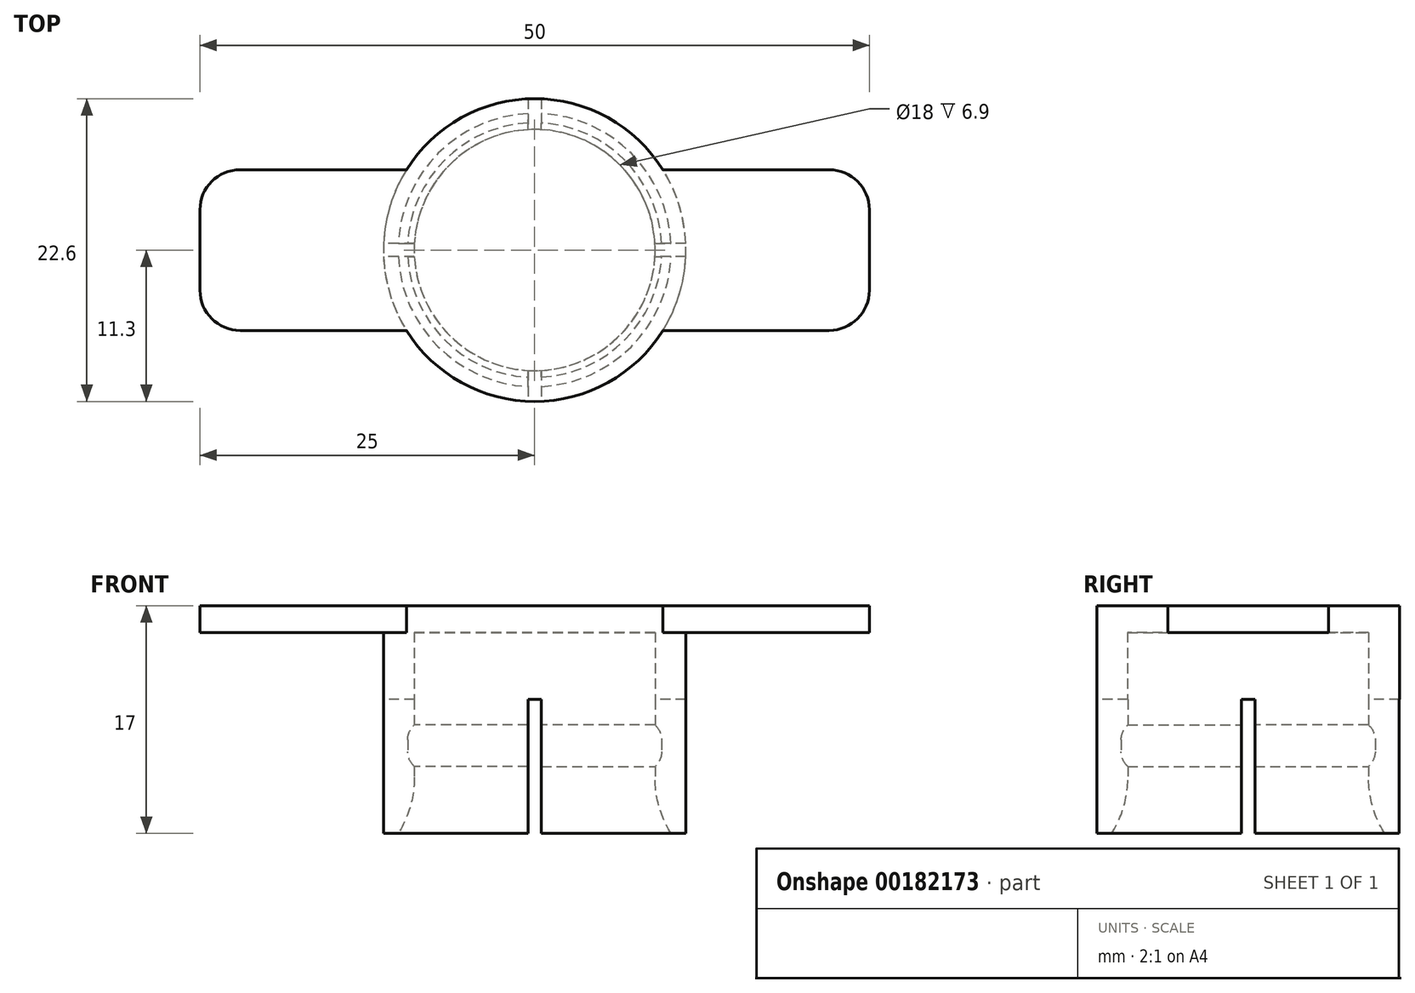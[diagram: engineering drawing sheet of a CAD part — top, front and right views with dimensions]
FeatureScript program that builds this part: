
annotation { "Feature Type Name" : "Feature", "Feature Type Description" : "" }
export const myFeature = defineFeature(function(context is Context, id is Id, definition is map)
    precondition{}
    {
        {
            var Q0;
            Q0=qCreatedBy(makeId("Top.planeOp"),FACE);
            var sketch = newSketch(context, id + "F0", { "sketchPlane" : qUnion([Q0])});
            skCircle(sketch, "E0", {"center": v(0, 0) * mm, "radius": 11.3 * mm});
            skCircle(sketch, "E1", {"center": v(0, 0) * mm, "radius": 9 * mm});
            skSolve(sketch);
        }
        {
            var Q0;
            Q0 = qSketchRegion(id + "F0", true);
            extrude(context, id + "F1", {"entities" : qUnion([Q0]), "depth" : 15 * mm});
        }
        {
            var Q0;
            Q0=makeQuery(id+"F1.opExtrude","CAP_FACE",FACE,{"disambiguationData":[OSD([sQuery(id+"F0.wireOp",EDGE,"E0"),sQuery(id+"F0.wireOp",EDGE,"E1")])],"isStart":false});
            var sketch = newSketch(context, id + "F2", { "sketchPlane" : qUnion([Q0])});
            skCircle(sketch, "E2.0", {"center": v(0, 0) * mm, "radius": 11.3 * mm});
            skSolve(sketch);
        }
        {
            var Q0;
            Q0 = qSketchRegion(id + "F2", true);
            extrude(context, id + "F3", {"entities" : qUnion([Q0]), "operationType" : NewBodyOperationType.ADD, "depth" : 2 * mm});
        }
        {
            var Q0;
            Q0=makeQuery(id+"F1.opExtrude","CAP_FACE",FACE,{"disambiguationData":[OSD([sQuery(id+"F0.wireOp",EDGE,"E0"),sQuery(id+"F0.wireOp",EDGE,"E1")])],"isStart":true});
            var sketch = newSketch(context, id + "F4", { "sketchPlane" : qUnion([Q0])});
            skCircle(sketch, "E3", {"center": v(0, 0) * mm, "radius": 9.5 * mm});
            skCircle(sketch, "E4", {"center": v(0, 0) * mm, "radius": 7.14 * mm});
            skSolve(sketch);
        }
        {
            var Q0;
            Q0 = qSketchRegion(id + "F4", true);
            extrude(context, id + "F5", {"entities" : qUnion([Q0]), "operationType" : NewBodyOperationType.REMOVE, "oppositeDirection" : true, "depth" : 8.1 * mm, "hasSecondDirection" : true, "secondDirectionOppositeDirection" : true, "secondDirectionDepth" : 5 * mm});
        }
        {
            var Q0;
            Q0=makeQuery(id+"F5.boolean.opBoolean","COPY",FACE,{"derivedFrom":makeQuery(id+"F5.opExtrude","SWEPT_FACE",FACE,{"disambiguationData":[OSD([sQuery(id+"F4.wireOp",EDGE,"E3")])]})});
            fillet(context, id + "F6", {"entities" : qUnion([Q0]), "radius" : 1.5 * mm, "tangentPropagation" : true, "allowEdgeOverflow" : false});
        }
        {
            var Q0;
            Q0=makeQuery(id+"F3.opExtrude","CAP_FACE",FACE,{"disambiguationData":[OSD([sQuery(id+"F2.wireOp",EDGE,"E2.0")])],"isStart":false});
            var sketch = newSketch(context, id + "F7", { "sketchPlane" : qUnion([Q0])});
            skLineSegment(sketch, "E5.bottom", {"start": v(25, -6) * mm, "end": v(-25, -6) * mm});
            skLineSegment(sketch, "E5.top", {"start": v(25, 6) * mm, "end": v(-25, 6) * mm});
            skLineSegment(sketch, "E5.left", {"start": v(25, -6) * mm, "end": v(25, 6) * mm});
            skLineSegment(sketch, "E5.right", {"start": v(-25, -6) * mm, "end": v(-25, 6) * mm});
            skPoint(sketch, "E5.middle", {"position": v(0, 0) * mm});
            skSolve(sketch);
        }
        {
            var Q0;
            Q0 = qSketchRegion(id + "F7", true);
            extrude(context, id + "F8", {"entities" : qUnion([Q0]), "operationType" : NewBodyOperationType.ADD, "oppositeDirection" : true, "depth" : 2 * mm});
        }
        {
            var Q0;
            Q0=makeQuery(id+"F8.opExtrude","SWEPT_EDGE",EDGE,{"disambiguationData":[OSD([sQuery(id+"F7.wireOp",EDGE,"E5.top"),sQuery(id+"F7.wireOp",EDGE,"E5.right")])]});
            var Q1;
            Q1=makeQuery(id+"F8.opExtrude","SWEPT_EDGE",EDGE,{"disambiguationData":[OSD([sQuery(id+"F7.wireOp",EDGE,"E5.bottom"),sQuery(id+"F7.wireOp",EDGE,"E5.right")])]});
            var Q2;
            Q2=makeQuery(id+"F8.opExtrude","SWEPT_EDGE",EDGE,{"disambiguationData":[OSD([sQuery(id+"F7.wireOp",EDGE,"E5.top"),sQuery(id+"F7.wireOp",EDGE,"E5.left")])]});
            var Q3;
            Q3=makeQuery(id+"F8.opExtrude","SWEPT_EDGE",EDGE,{"disambiguationData":[OSD([sQuery(id+"F7.wireOp",EDGE,"E5.bottom"),sQuery(id+"F7.wireOp",EDGE,"E5.left")])]});
            fillet(context, id + "F9", {"entities" : qUnion([Q0, Q1, Q2, Q3]), "radius" : 3 * mm, "tangentPropagation" : true, "allowEdgeOverflow" : false});
        }
        {
            var Q0;
            Q0=makeQuery(id+"F1.opExtrude","CAP_FACE",FACE,{"disambiguationData":[OSD([sQuery(id+"F0.wireOp",EDGE,"E0"),sQuery(id+"F0.wireOp",EDGE,"E1")])],"isStart":true});
            var sketch = newSketch(context, id + "F10", { "sketchPlane" : qUnion([Q0])});
            skLineSegment(sketch, "E6.bottom", {"start": v(-0.5, -12.5) * mm, "end": v(0.5, -12.5) * mm});
            skLineSegment(sketch, "E6.top", {"start": v(-0.5, 12.5) * mm, "end": v(0.5, 12.5) * mm});
            skLineSegment(sketch, "E6.left", {"start": v(-0.5, -12.5) * mm, "end": v(-0.5, 12.5) * mm});
            skLineSegment(sketch, "E6.right", {"start": v(0.5, -12.5) * mm, "end": v(0.5, 12.5) * mm});
            skPoint(sketch, "E6.middle", {"position": v(0, 0) * mm});
            skLineSegment(sketch, "E7.bottom", {"start": v(12.5, 0.5) * mm, "end": v(-12.5, 0.5) * mm});
            skLineSegment(sketch, "E7.top", {"start": v(12.5, -0.5) * mm, "end": v(-12.5, -0.5) * mm});
            skLineSegment(sketch, "E7.left", {"start": v(12.5, 0.5) * mm, "end": v(12.5, -0.5) * mm});
            skLineSegment(sketch, "E7.right", {"start": v(-12.5, 0.5) * mm, "end": v(-12.5, -0.5) * mm});
            skSolve(sketch);
        }
        {
            var Q0;
            Q0 = qSketchRegion(id + "F10", true);
            extrude(context, id + "F11", {"entities" : qUnion([Q0]), "operationType" : NewBodyOperationType.REMOVE, "oppositeDirection" : true, "depth" : 10 * mm});
        }
        {
            var Q0;
            {var subQ0=sQuery(id+"F0.wireOp",EDGE,"E1");var subQ1=sQuery(id+"F0.wireOp",EDGE,"E0");var subQ2=sQuery(id+"F10.wireOp",EDGE,"E7.bottom");var subQ3=sQuery(id+"F10.wireOp",EDGE,"E6.right");var subQ4=makeQuery(id+"F10.imprint","INTERSECT",VERTEX,{"derivedFrom":[subQ3,subQ2]});var subQ5=makeQuery(id+"F1.opExtrude","CAP_EDGE",EDGE,{"disambiguationData":[OSD([subQ0])],"isStart":true});var subQ7=makeQuery(id+"F1.opExtrude","CAP_EDGE",EDGE,{"disambiguationData":[OSD([subQ1])],"isStart":true});var subQ9=makeQuery(id+"F10.imprint","INTERSECT",VERTEX,{"disambiguationData":[OD(1.0)],"derivedFrom":[subQ7,subQ3]});Q0=makeQuery(id+"F11.boolean.opBoolean","SPLIT",EDGE,{"disambiguationData":[TD([makeQuery(id+"F11.opExtrude","SWEPT_FACE",FACE,{"disambiguationData":[OSD([subQ3]),TDD([makeQuery(id+"F10.imprint","IMPRINT",EDGE,{"disambiguationData":[TD([[subQ4,-1.0]])],"derivedFrom":subQ3}),makeQuery(id+"F10.imprint","IMPRINT",EDGE,{"disambiguationData":[TD([[subQ9,1.0]])],"derivedFrom":subQ3}),makeQuery(id+"F10.imprint","IMPRINT",EDGE,{"disambiguationData":[TD([[makeQuery(id+"F10.imprint","INTERSECT",VERTEX,{"derivedFrom":[sQuery(id+"F10.wireOp",EDGE,"E6.top"),subQ3]}),1.0]])],"derivedFrom":subQ3})])]})])],"derivedFrom":subQ5});}
            var Q1;
            {var subQ0=sQuery(id+"F0.wireOp",EDGE,"E1");var subQ1=sQuery(id+"F0.wireOp",EDGE,"E0");var subQ2=sQuery(id+"F10.wireOp",EDGE,"E7.top");var subQ3=sQuery(id+"F10.wireOp",EDGE,"E6.right");var subQ4=makeQuery(id+"F10.imprint","INTERSECT",VERTEX,{"derivedFrom":[subQ3,subQ2]});var subQ5=makeQuery(id+"F1.opExtrude","CAP_EDGE",EDGE,{"disambiguationData":[OSD([subQ0])],"isStart":true});var subQ7=makeQuery(id+"F1.opExtrude","CAP_EDGE",EDGE,{"disambiguationData":[OSD([subQ1])],"isStart":true});var subQ10=makeQuery(id+"F10.imprint","INTERSECT",VERTEX,{"disambiguationData":[OD(0.0)],"derivedFrom":[subQ7,subQ3]});Q1=makeQuery(id+"F11.boolean.opBoolean","SPLIT",EDGE,{"disambiguationData":[TD([makeQuery(id+"F11.opExtrude","SWEPT_FACE",FACE,{"disambiguationData":[OSD([subQ3]),TDD([makeQuery(id+"F10.imprint","IMPRINT",EDGE,{"disambiguationData":[TD([[makeQuery(id+"F10.imprint","INTERSECT",VERTEX,{"derivedFrom":[sQuery(id+"F10.wireOp",EDGE,"E6.bottom"),subQ3]}),-1.0]])],"derivedFrom":subQ3}),makeQuery(id+"F10.imprint","IMPRINT",EDGE,{"disambiguationData":[TD([[subQ10,-1.0]])],"derivedFrom":subQ3}),makeQuery(id+"F10.imprint","IMPRINT",EDGE,{"disambiguationData":[TD([[subQ4,1.0]])],"derivedFrom":subQ3})])]})])],"derivedFrom":subQ5});}
            var Q2;
            {var subQ0=sQuery(id+"F0.wireOp",EDGE,"E1");var subQ1=sQuery(id+"F0.wireOp",EDGE,"E0");var subQ2=sQuery(id+"F10.wireOp",EDGE,"E6.left");var subQ3=makeQuery(id+"F1.opExtrude","CAP_EDGE",EDGE,{"disambiguationData":[OSD([subQ1])],"isStart":true});var subQ4=makeQuery(id+"F10.imprint","INTERSECT",VERTEX,{"disambiguationData":[OD(1.0)],"derivedFrom":[subQ3,subQ2]});var subQ5=makeQuery(id+"F1.opExtrude","CAP_EDGE",EDGE,{"disambiguationData":[OSD([subQ0])],"isStart":true});var subQ7=sQuery(id+"F10.wireOp",EDGE,"E7.bottom");var subQ8=makeQuery(id+"F10.imprint","INTERSECT",VERTEX,{"derivedFrom":[subQ2,subQ7]});Q2=makeQuery(id+"F11.boolean.opBoolean","SPLIT",EDGE,{"disambiguationData":[TD([makeQuery(id+"F11.opExtrude","SWEPT_FACE",FACE,{"disambiguationData":[OSD([subQ2]),TDD([makeQuery(id+"F10.imprint","IMPRINT",EDGE,{"disambiguationData":[TD([[subQ8,-1.0]])],"derivedFrom":subQ2}),makeQuery(id+"F10.imprint","IMPRINT",EDGE,{"disambiguationData":[TD([[subQ4,1.0]])],"derivedFrom":subQ2}),makeQuery(id+"F10.imprint","IMPRINT",EDGE,{"disambiguationData":[TD([[makeQuery(id+"F10.imprint","INTERSECT",VERTEX,{"derivedFrom":[sQuery(id+"F10.wireOp",EDGE,"E6.top"),subQ2]}),1.0]])],"derivedFrom":subQ2})])]})])],"derivedFrom":subQ5});}
            var Q3;
            {var subQ0=sQuery(id+"F0.wireOp",EDGE,"E1");var subQ1=sQuery(id+"F0.wireOp",EDGE,"E0");var subQ2=sQuery(id+"F10.wireOp",EDGE,"E7.top");var subQ3=sQuery(id+"F10.wireOp",EDGE,"E6.left");var subQ4=makeQuery(id+"F10.imprint","INTERSECT",VERTEX,{"derivedFrom":[subQ3,subQ2]});var subQ5=makeQuery(id+"F1.opExtrude","CAP_EDGE",EDGE,{"disambiguationData":[OSD([subQ0])],"isStart":true});var subQ7=makeQuery(id+"F1.opExtrude","CAP_EDGE",EDGE,{"disambiguationData":[OSD([subQ1])],"isStart":true});var subQ8=makeQuery(id+"F10.imprint","INTERSECT",VERTEX,{"disambiguationData":[OD(0.0)],"derivedFrom":[subQ7,subQ3]});Q3=makeQuery(id+"F11.boolean.opBoolean","SPLIT",EDGE,{"disambiguationData":[TD([makeQuery(id+"F11.opExtrude","SWEPT_FACE",FACE,{"disambiguationData":[OSD([subQ3]),TDD([makeQuery(id+"F10.imprint","IMPRINT",EDGE,{"disambiguationData":[TD([[makeQuery(id+"F10.imprint","INTERSECT",VERTEX,{"derivedFrom":[sQuery(id+"F10.wireOp",EDGE,"E6.bottom"),subQ3]}),-1.0]])],"derivedFrom":subQ3}),makeQuery(id+"F10.imprint","IMPRINT",EDGE,{"disambiguationData":[TD([[subQ8,-1.0]])],"derivedFrom":subQ3}),makeQuery(id+"F10.imprint","IMPRINT",EDGE,{"disambiguationData":[TD([[subQ4,1.0]])],"derivedFrom":subQ3})])]})])],"derivedFrom":subQ5});}
            chamfer(context, id + "F12", {"entities" : qUnion([Q0, Q1, Q2, Q3]), "width" : 1.2 * mm});
        }
        {
            var Q0;
            {var subQ0=sQuery(id+"F0.wireOp",EDGE,"E1");var subQ1=sQuery(id+"F0.wireOp",EDGE,"E0");var subQ2=makeQuery(id+"F1.opExtrude","CAP_FACE",FACE,{"disambiguationData":[OSD([subQ1,subQ0])],"isStart":true});var subQ4=sQuery(id+"F10.wireOp",EDGE,"E7.bottom");var subQ5=makeQuery(id+"F1.opExtrude","CAP_EDGE",EDGE,{"disambiguationData":[OSD([subQ1])],"isStart":true});var subQ7=makeQuery(id+"F1.opExtrude","CAP_EDGE",EDGE,{"disambiguationData":[OSD([subQ0])],"isStart":true});var subQ9=sQuery(id+"F10.wireOp",EDGE,"E6.left");var subQ10=makeQuery(id+"F10.imprint","INTERSECT",VERTEX,{"derivedFrom":[subQ9,subQ4]});var subQ12=makeQuery(id+"F10.imprint","INTERSECT",VERTEX,{"disambiguationData":[OD(1.0)],"derivedFrom":[subQ5,subQ9]});var subQ14=makeQuery(id+"F11.opExtrude","SWEPT_FACE",FACE,{"disambiguationData":[OSD([subQ9]),TDD([makeQuery(id+"F10.imprint","IMPRINT",EDGE,{"disambiguationData":[TD([[subQ10,-1.0]])],"derivedFrom":subQ9}),makeQuery(id+"F10.imprint","IMPRINT",EDGE,{"disambiguationData":[TD([[subQ12,1.0]])],"derivedFrom":subQ9}),makeQuery(id+"F10.imprint","IMPRINT",EDGE,{"disambiguationData":[TD([[makeQuery(id+"F10.imprint","INTERSECT",VERTEX,{"derivedFrom":[sQuery(id+"F10.wireOp",EDGE,"E6.top"),subQ9]}),1.0]])],"derivedFrom":subQ9})])]});var subQ15=makeQuery(id+"F1.opExtrude","SWEPT_FACE",FACE,{"disambiguationData":[OSD([subQ0])]});Q0=makeQuery(id+"F12.opChamfer","BLEND_EDGE",EDGE,{"blendedFrom":[makeQuery(id+"F11.boolean.opBoolean","SPLIT",EDGE,{"disambiguationData":[TD([subQ14])],"derivedFrom":subQ7}),makeQuery(id+"F11.boolean.opBoolean","SPLIT",FACE,{"disambiguationData":[TD([subQ14])],"derivedFrom":makeQuery(id+"F5.boolean.opBoolean","SPLIT",FACE,{"disambiguationData":[TD([subQ2])],"derivedFrom":subQ15})})],"blendedInto":[makeQuery(id+"F11.boolean.opBoolean","SPLIT",FACE,{"disambiguationData":[TD([subQ14])],"derivedFrom":makeQuery(id+"F5.boolean.opBoolean","SPLIT",FACE,{"disambiguationData":[TD([subQ2])],"derivedFrom":subQ15})})]});}
            var Q1;
            {var subQ0=sQuery(id+"F0.wireOp",EDGE,"E1");var subQ1=sQuery(id+"F0.wireOp",EDGE,"E0");var subQ2=makeQuery(id+"F1.opExtrude","CAP_FACE",FACE,{"disambiguationData":[OSD([subQ1,subQ0])],"isStart":true});var subQ3=sQuery(id+"F10.wireOp",EDGE,"E7.bottom");var subQ4=sQuery(id+"F10.wireOp",EDGE,"E6.right");var subQ5=makeQuery(id+"F10.imprint","INTERSECT",VERTEX,{"derivedFrom":[subQ4,subQ3]});var subQ6=makeQuery(id+"F1.opExtrude","CAP_EDGE",EDGE,{"disambiguationData":[OSD([subQ0])],"isStart":true});var subQ8=makeQuery(id+"F1.opExtrude","CAP_EDGE",EDGE,{"disambiguationData":[OSD([subQ1])],"isStart":true});var subQ12=makeQuery(id+"F10.imprint","INTERSECT",VERTEX,{"disambiguationData":[OD(1.0)],"derivedFrom":[subQ8,subQ4]});var subQ14=makeQuery(id+"F11.opExtrude","SWEPT_FACE",FACE,{"disambiguationData":[OSD([subQ4]),TDD([makeQuery(id+"F10.imprint","IMPRINT",EDGE,{"disambiguationData":[TD([[subQ5,-1.0]])],"derivedFrom":subQ4}),makeQuery(id+"F10.imprint","IMPRINT",EDGE,{"disambiguationData":[TD([[subQ12,1.0]])],"derivedFrom":subQ4}),makeQuery(id+"F10.imprint","IMPRINT",EDGE,{"disambiguationData":[TD([[makeQuery(id+"F10.imprint","INTERSECT",VERTEX,{"derivedFrom":[sQuery(id+"F10.wireOp",EDGE,"E6.top"),subQ4]}),1.0]])],"derivedFrom":subQ4})])]});var subQ15=makeQuery(id+"F1.opExtrude","SWEPT_FACE",FACE,{"disambiguationData":[OSD([subQ0])]});Q1=makeQuery(id+"F12.opChamfer","BLEND_EDGE",EDGE,{"blendedFrom":[makeQuery(id+"F11.boolean.opBoolean","SPLIT",EDGE,{"disambiguationData":[TD([subQ14])],"derivedFrom":subQ6}),makeQuery(id+"F11.boolean.opBoolean","SPLIT",FACE,{"disambiguationData":[TD([subQ14])],"derivedFrom":makeQuery(id+"F5.boolean.opBoolean","SPLIT",FACE,{"disambiguationData":[TD([subQ2])],"derivedFrom":subQ15})})],"blendedInto":[makeQuery(id+"F11.boolean.opBoolean","SPLIT",FACE,{"disambiguationData":[TD([subQ14])],"derivedFrom":makeQuery(id+"F5.boolean.opBoolean","SPLIT",FACE,{"disambiguationData":[TD([subQ2])],"derivedFrom":subQ15})})]});}
            var Q2;
            {var subQ0=sQuery(id+"F0.wireOp",EDGE,"E1");var subQ1=sQuery(id+"F0.wireOp",EDGE,"E0");var subQ2=makeQuery(id+"F1.opExtrude","CAP_FACE",FACE,{"disambiguationData":[OSD([subQ1,subQ0])],"isStart":true});var subQ4=sQuery(id+"F10.wireOp",EDGE,"E7.top");var subQ5=sQuery(id+"F10.wireOp",EDGE,"E6.right");var subQ6=makeQuery(id+"F10.imprint","INTERSECT",VERTEX,{"derivedFrom":[subQ5,subQ4]});var subQ7=makeQuery(id+"F1.opExtrude","CAP_EDGE",EDGE,{"disambiguationData":[OSD([subQ0])],"isStart":true});var subQ9=makeQuery(id+"F1.opExtrude","CAP_EDGE",EDGE,{"disambiguationData":[OSD([subQ1])],"isStart":true});var subQ10=makeQuery(id+"F10.imprint","INTERSECT",VERTEX,{"disambiguationData":[OD(0.0)],"derivedFrom":[subQ9,subQ5]});var subQ11=makeQuery(id+"F11.opExtrude","SWEPT_FACE",FACE,{"disambiguationData":[OSD([subQ5]),TDD([makeQuery(id+"F10.imprint","IMPRINT",EDGE,{"disambiguationData":[TD([[makeQuery(id+"F10.imprint","INTERSECT",VERTEX,{"derivedFrom":[sQuery(id+"F10.wireOp",EDGE,"E6.bottom"),subQ5]}),-1.0]])],"derivedFrom":subQ5}),makeQuery(id+"F10.imprint","IMPRINT",EDGE,{"disambiguationData":[TD([[subQ10,-1.0]])],"derivedFrom":subQ5}),makeQuery(id+"F10.imprint","IMPRINT",EDGE,{"disambiguationData":[TD([[subQ6,1.0]])],"derivedFrom":subQ5})])]});var subQ15=makeQuery(id+"F1.opExtrude","SWEPT_FACE",FACE,{"disambiguationData":[OSD([subQ0])]});Q2=makeQuery(id+"F12.opChamfer","BLEND_EDGE",EDGE,{"blendedFrom":[makeQuery(id+"F11.boolean.opBoolean","SPLIT",EDGE,{"disambiguationData":[TD([subQ11])],"derivedFrom":subQ7}),makeQuery(id+"F11.boolean.opBoolean","SPLIT",FACE,{"disambiguationData":[TD([subQ11])],"derivedFrom":makeQuery(id+"F5.boolean.opBoolean","SPLIT",FACE,{"disambiguationData":[TD([subQ2])],"derivedFrom":subQ15})})],"blendedInto":[makeQuery(id+"F11.boolean.opBoolean","SPLIT",FACE,{"disambiguationData":[TD([subQ11])],"derivedFrom":makeQuery(id+"F5.boolean.opBoolean","SPLIT",FACE,{"disambiguationData":[TD([subQ2])],"derivedFrom":subQ15})})]});}
            var Q3;
            {var subQ0=sQuery(id+"F0.wireOp",EDGE,"E1");var subQ1=sQuery(id+"F0.wireOp",EDGE,"E0");var subQ2=makeQuery(id+"F1.opExtrude","CAP_FACE",FACE,{"disambiguationData":[OSD([subQ1,subQ0])],"isStart":true});var subQ4=sQuery(id+"F10.wireOp",EDGE,"E7.top");var subQ5=sQuery(id+"F10.wireOp",EDGE,"E6.left");var subQ6=makeQuery(id+"F10.imprint","INTERSECT",VERTEX,{"derivedFrom":[subQ5,subQ4]});var subQ7=makeQuery(id+"F1.opExtrude","CAP_EDGE",EDGE,{"disambiguationData":[OSD([subQ0])],"isStart":true});var subQ9=makeQuery(id+"F1.opExtrude","CAP_EDGE",EDGE,{"disambiguationData":[OSD([subQ1])],"isStart":true});var subQ10=makeQuery(id+"F10.imprint","INTERSECT",VERTEX,{"disambiguationData":[OD(0.0)],"derivedFrom":[subQ9,subQ5]});var subQ11=makeQuery(id+"F11.opExtrude","SWEPT_FACE",FACE,{"disambiguationData":[OSD([subQ5]),TDD([makeQuery(id+"F10.imprint","IMPRINT",EDGE,{"disambiguationData":[TD([[makeQuery(id+"F10.imprint","INTERSECT",VERTEX,{"derivedFrom":[sQuery(id+"F10.wireOp",EDGE,"E6.bottom"),subQ5]}),-1.0]])],"derivedFrom":subQ5}),makeQuery(id+"F10.imprint","IMPRINT",EDGE,{"disambiguationData":[TD([[subQ10,-1.0]])],"derivedFrom":subQ5}),makeQuery(id+"F10.imprint","IMPRINT",EDGE,{"disambiguationData":[TD([[subQ6,1.0]])],"derivedFrom":subQ5})])]});var subQ15=makeQuery(id+"F1.opExtrude","SWEPT_FACE",FACE,{"disambiguationData":[OSD([subQ0])]});Q3=makeQuery(id+"F12.opChamfer","BLEND_EDGE",EDGE,{"blendedFrom":[makeQuery(id+"F11.boolean.opBoolean","SPLIT",EDGE,{"disambiguationData":[TD([subQ11])],"derivedFrom":subQ7}),makeQuery(id+"F11.boolean.opBoolean","SPLIT",FACE,{"disambiguationData":[TD([subQ11])],"derivedFrom":makeQuery(id+"F5.boolean.opBoolean","SPLIT",FACE,{"disambiguationData":[TD([subQ2])],"derivedFrom":subQ15})})],"blendedInto":[makeQuery(id+"F11.boolean.opBoolean","SPLIT",FACE,{"disambiguationData":[TD([subQ11])],"derivedFrom":makeQuery(id+"F5.boolean.opBoolean","SPLIT",FACE,{"disambiguationData":[TD([subQ2])],"derivedFrom":subQ15})})]});}
            fillet(context, id + "F13", {"entities" : qUnion([Q0, Q1, Q2, Q3]), "radius" : 8 * mm, "tangentPropagation" : true, "allowEdgeOverflow" : false});
        }
    });
